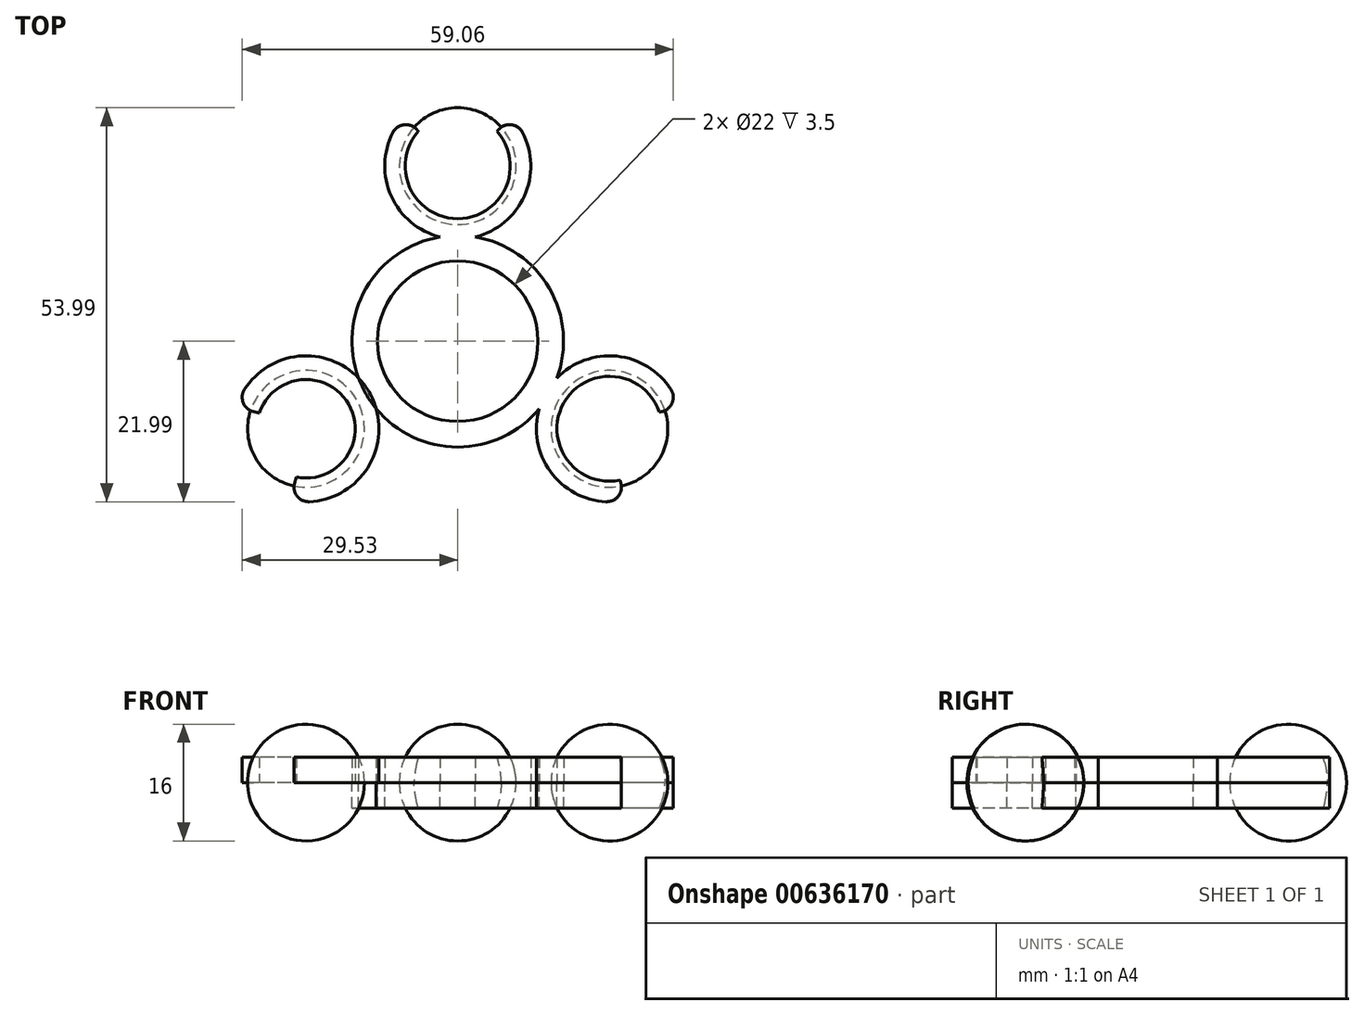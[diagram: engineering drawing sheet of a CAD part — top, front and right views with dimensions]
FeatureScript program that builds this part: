
annotation { "Feature Type Name" : "Feature", "Feature Type Description" : "" }
export const myFeature = defineFeature(function(context is Context, id is Id, definition is map)
    precondition{}
    {
        {
            var Q0;
            Q0=qCreatedBy(makeId("Top.planeOp"),FACE);
            var sketch = newSketch(context, id + "F0", { "sketchPlane" : qUnion([Q0])});
            skCircle(sketch, "E0", {"center": v(0, 0) * mm, "radius": 11 * mm});
            skCircle(sketch, "E1", {"center": v(0, 0) * mm, "radius": 14.5 * mm});
            skArc(sketch, "E2", {"start": v(-5.06, 28.47) * mm, "mid": v(0, 17.25) * mm, "end": v(5.06, 28.47) * mm});
            skArc(sketch, "E3", {"start": v(-6.95, 31.19) * mm, "mid": v(0, 14) * mm, "end": v(6.95, 31.19) * mm});
            skArc(sketch, "E4.1.0", {"start": v(-23.53, -21.61) * mm, "mid": v(-12.12, -7) * mm, "end": v(-30.49, -9.57) * mm});
            skArc(sketch, "E4.1.1", {"start": v(-22.12, -18.62) * mm, "mid": v(-14.94, -8.62) * mm, "end": v(-27.18, -9.85) * mm});
            skArc(sketch, "E4.2.0", {"start": v(30.49, -9.57) * mm, "mid": v(12.12, -7) * mm, "end": v(23.53, -21.61) * mm});
            skArc(sketch, "E4.2.1", {"start": v(27.18, -9.85) * mm, "mid": v(14.94, -8.63) * mm, "end": v(22.12, -18.62) * mm});
            skArc(sketch, "E5", {"start": v(-6.95, 31.19) * mm, "mid": v(-6.16, 29.72) * mm, "end": v(-5.06, 28.47) * mm});
            skArc(sketch, "E6.trimOffspring", {"start": v(5.06, 28.47) * mm, "mid": v(6.16, 29.72) * mm, "end": v(6.95, 31.19) * mm});
            skArc(sketch, "E7.1.0", {"start": v(-27.18, -9.85) * mm, "mid": v(-28.82, -9.53) * mm, "end": v(-30.49, -9.57) * mm});
            skArc(sketch, "E7.1.1", {"start": v(-23.53, -21.61) * mm, "mid": v(-22.66, -20.2) * mm, "end": v(-22.12, -18.62) * mm});
            skArc(sketch, "E7.2.0", {"start": v(22.12, -18.62) * mm, "mid": v(22.66, -20.2) * mm, "end": v(23.53, -21.61) * mm});
            skArc(sketch, "E7.2.1", {"start": v(30.49, -9.57) * mm, "mid": v(28.82, -9.53) * mm, "end": v(27.18, -9.85) * mm});
            skCircle(sketch, "E8", {"center": v(0, 24) * mm, "radius": 8 * mm});
            skLineSegment(sketch, "E9", {"start": v(0, 28.85) * mm, "end": v(0, 20.31) * mm, "construction": true});
            skLineSegment(sketch, "E10", {"start": v(0, 32) * mm, "end": v(0, 16) * mm});
            skPoint(sketch, "E10.endSnap0", {"position": v(0, 17.25) * mm});
            skSolve(sketch);
        }
        {
            var Q0;
            Q0=makeQuery(id+"F0.imprint","IMPRINT",FACE,{"disambiguationData":[TD([[makeQuery(id+"F0.imprint","IMPRINT",EDGE,{"derivedFrom":sQuery(id+"F0.wireOp",EDGE,"E4.1.1")}),-1.0]])]});
            var Q1;
            {var subQ0=sQuery(id+"F0.wireOp",EDGE,"E4.1.0");var subQ1=sQuery(id+"F0.wireOp",EDGE,"E0");var subQ2=makeQuery(id+"F0.imprint","INTERSECT",VERTEX,{"derivedFrom":[subQ1,subQ0]});Q1=makeQuery(id+"F0.imprint","IMPRINT",FACE,{"disambiguationData":[TD([[makeQuery(id+"F0.imprint","IMPRINT",EDGE,{"disambiguationData":[TD([[subQ2,1.0]])],"derivedFrom":subQ1}),-1.0]])]});}
            var Q2;
            {var subQ0=sQuery(id+"F0.wireOp",EDGE,"E4.1.0");var subQ1=sQuery(id+"F0.wireOp",EDGE,"E1");var subQ2=makeQuery(id+"F0.imprint","INTERSECT",VERTEX,{"disambiguationData":[OD(0.0)],"derivedFrom":[subQ1,subQ0]});Q2=makeQuery(id+"F0.imprint","IMPRINT",FACE,{"disambiguationData":[TD([[makeQuery(id+"F0.imprint","IMPRINT",EDGE,{"disambiguationData":[TD([[subQ2,-1.0]])],"derivedFrom":subQ1}),1.0]])]});}
            var Q3;
            {var subQ0=sQuery(id+"F0.wireOp",EDGE,"E4.1.0");var subQ1=sQuery(id+"F0.wireOp",EDGE,"E0");var subQ2=makeQuery(id+"F0.imprint","INTERSECT",VERTEX,{"derivedFrom":[subQ1,subQ0]});Q3=makeQuery(id+"F0.imprint","IMPRINT",FACE,{"disambiguationData":[TD([[makeQuery(id+"F0.imprint","IMPRINT",EDGE,{"disambiguationData":[TD([[subQ2,-1.0]])],"derivedFrom":subQ1}),-1.0]])]});}
            var Q4;
            {var subQ0=sQuery(id+"F0.wireOp",EDGE,"E4.2.0");var subQ1=sQuery(id+"F0.wireOp",EDGE,"E1");var subQ2=makeQuery(id+"F0.imprint","INTERSECT",VERTEX,{"disambiguationData":[OD(0.0)],"derivedFrom":[subQ1,subQ0]});Q4=makeQuery(id+"F0.imprint","IMPRINT",FACE,{"disambiguationData":[TD([[makeQuery(id+"F0.imprint","IMPRINT",EDGE,{"disambiguationData":[TD([[subQ2,-1.0]])],"derivedFrom":subQ1}),1.0]])]});}
            var Q5;
            Q5=makeQuery(id+"F0.imprint","IMPRINT",FACE,{"disambiguationData":[TD([[makeQuery(id+"F0.imprint","IMPRINT",EDGE,{"derivedFrom":sQuery(id+"F0.wireOp",EDGE,"E4.2.1")}),-1.0]])]});
            var Q6;
            {var subQ0=sQuery(id+"F0.wireOp",EDGE,"E3");var subQ1=sQuery(id+"F0.wireOp",EDGE,"E0");var subQ2=makeQuery(id+"F0.imprint","INTERSECT",VERTEX,{"derivedFrom":[subQ1,subQ0]});Q6=makeQuery(id+"F0.imprint","IMPRINT",FACE,{"disambiguationData":[TD([[makeQuery(id+"F0.imprint","IMPRINT",EDGE,{"disambiguationData":[TD([[subQ2,1.0]])],"derivedFrom":subQ1}),-1.0]])]});}
            var Q7;
            {var subQ0=sQuery(id+"F0.wireOp",EDGE,"E3");var subQ1=sQuery(id+"F0.wireOp",EDGE,"E1");var subQ2=makeQuery(id+"F0.imprint","INTERSECT",VERTEX,{"disambiguationData":[OD(0.0)],"derivedFrom":[subQ1,subQ0]});Q7=makeQuery(id+"F0.imprint","IMPRINT",FACE,{"disambiguationData":[TD([[makeQuery(id+"F0.imprint","IMPRINT",EDGE,{"disambiguationData":[TD([[subQ2,1.0]])],"derivedFrom":subQ1}),1.0]])]});}
            var Q8;
            Q8=makeQuery(id+"F0.imprint","IMPRINT",FACE,{"disambiguationData":[TD([[makeQuery(id+"F0.imprint","IMPRINT",EDGE,{"derivedFrom":sQuery(id+"F0.wireOp",EDGE,"E2")}),-1.0]])]});
            var Q9;
            {var subQ1=sQuery(id+"F0.wireOp",EDGE,"E3");var subQ5=sQuery(id+"F0.wireOp",EDGE,"E1");var subQ6=makeQuery(id+"F0.imprint","INTERSECT",VERTEX,{"disambiguationData":[OD(0.0)],"derivedFrom":[subQ5,subQ1]});Q9=makeQuery(id+"F0.imprint","IMPRINT",FACE,{"disambiguationData":[TD([[makeQuery(id+"F0.imprint","IMPRINT",EDGE,{"disambiguationData":[TD([[subQ6,1.0]])],"derivedFrom":subQ5}),-1.0]])]});}
            extrude(context, id + "F1", {"entities" : qUnion([Q0, Q1, Q2, Q3, Q4, Q5, Q6, Q7, Q8, Q9]), "depth" : 3.5 * mm, "offsetDistance" : 25 * mm});
        }
        {
            var Q0;
            {var subQ0=sQuery(id+"F0.wireOp",EDGE,"E6.trimOffspring");var subQ1=sQuery(id+"F0.wireOp",EDGE,"E2");var subQ2=makeQuery(id+"F0.imprint","INTERSECT",VERTEX,{"derivedFrom":[subQ1,subQ0]});Q0=makeQuery(id+"F0.imprint","IMPRINT",FACE,{"disambiguationData":[TD([[makeQuery(id+"F0.imprint","IMPRINT",EDGE,{"disambiguationData":[TD([[subQ2,1.0]])],"derivedFrom":subQ1}),1.0]])]});}
            var Q1;
            {var subQ0=sQuery(id+"F0.wireOp",EDGE,"E6.trimOffspring");var subQ1=sQuery(id+"F0.wireOp",EDGE,"E2");var subQ2=makeQuery(id+"F0.imprint","INTERSECT",VERTEX,{"derivedFrom":[subQ1,subQ0]});Q1=makeQuery(id+"F0.imprint","IMPRINT",FACE,{"disambiguationData":[TD([[makeQuery(id+"F0.imprint","IMPRINT",EDGE,{"disambiguationData":[TD([[subQ2,1.0]])],"derivedFrom":subQ1}),-1.0]])]});}
            var Q2;
            Q2=sQuery(id+"F0.wireOp",EDGE,"E10");
            revolve(context, id + "F2", {"entities" : qUnion([Q0, Q1]), "axis" : qUnion([Q2]), "revolveType" : RevolveType.FULL});
        }
        {
            var Q0;
            Q0=makeQuery(id+"F2.opRevolve","SWEPT_BODY",BODY,{"disambiguationData":[OSD([sQuery(id+"F0.wireOp",EDGE,"E8"),sQuery(id+"F0.wireOp",EDGE,"E10")])]});
            var Q1;
            Q1=sQuery(id+"F0.wireOp",EDGE,"E0");
            circularPattern(context, id + "F3", {"entities" : qUnion([Q0]), "axis" : qUnion([Q1]), "angle" : 360 * degree, "instanceCount" : 3, "equalSpace" : true});
        }
        {
            var Q0;
            Q0=makeQuery(id+"F2.opRevolve","SWEPT_BODY",BODY,{"disambiguationData":[OSD([sQuery(id+"F0.wireOp",EDGE,"E8"),sQuery(id+"F0.wireOp",EDGE,"E10")])]});
            var Q1;
            Q1=makeQuery(id+"F3.opPattern","COPY",BODY,{"derivedFrom":makeQuery(id+"F2.opRevolve","SWEPT_BODY",BODY,{"disambiguationData":[OSD([sQuery(id+"F0.wireOp",EDGE,"E8"),sQuery(id+"F0.wireOp",EDGE,"E10")])]}),"instanceName":"1"});
            var Q2;
            Q2=makeQuery(id+"F3.opPattern","COPY",BODY,{"derivedFrom":makeQuery(id+"F2.opRevolve","SWEPT_BODY",BODY,{"disambiguationData":[OSD([sQuery(id+"F0.wireOp",EDGE,"E8"),sQuery(id+"F0.wireOp",EDGE,"E10")])]}),"instanceName":"2"});
            var Q3;
            Q3=makeQuery(id+"F1.opExtrude","SWEPT_BODY",BODY,{"disambiguationData":[OSD([sQuery(id+"F0.wireOp",EDGE,"E0"),sQuery(id+"F0.wireOp",EDGE,"E1"),sQuery(id+"F0.wireOp",EDGE,"E2"),sQuery(id+"F0.wireOp",EDGE,"E3"),sQuery(id+"F0.wireOp",EDGE,"E4.1.0"),sQuery(id+"F0.wireOp",EDGE,"E4.1.1"),sQuery(id+"F0.wireOp",EDGE,"E4.2.0"),sQuery(id+"F0.wireOp",EDGE,"E4.2.1"),sQuery(id+"F0.wireOp",EDGE,"E5"),sQuery(id+"F0.wireOp",EDGE,"E6.trimOffspring"),sQuery(id+"F0.wireOp",EDGE,"E7.1.0"),sQuery(id+"F0.wireOp",EDGE,"E7.1.1"),sQuery(id+"F0.wireOp",EDGE,"E7.2.0"),sQuery(id+"F0.wireOp",EDGE,"E7.2.1")])]});
            var Q4;
            {var subQ0=sQuery(id+"F0.wireOp",EDGE,"E7.2.1");var subQ1=sQuery(id+"F0.wireOp",EDGE,"E7.2.0");var subQ2=sQuery(id+"F0.wireOp",EDGE,"E7.1.1");var subQ3=sQuery(id+"F0.wireOp",EDGE,"E7.1.0");var subQ4=sQuery(id+"F0.wireOp",EDGE,"E6.trimOffspring");var subQ5=sQuery(id+"F0.wireOp",EDGE,"E3");var subQ6=makeQuery(id+"F0.imprint","INTERSECT",VERTEX,{"derivedFrom":[subQ5,subQ4]});var subQ9=sQuery(id+"F0.wireOp",EDGE,"E2");var subQ10=makeQuery(id+"F0.imprint","INTERSECT",VERTEX,{"derivedFrom":[subQ9,subQ4]});var subQ11=sQuery(id+"F0.wireOp",EDGE,"E5");var subQ12=makeQuery(id+"F0.imprint","INTERSECT",VERTEX,{"derivedFrom":[subQ9,subQ11]});var subQ14=makeQuery(id+"F0.imprint","INTERSECT",VERTEX,{"derivedFrom":[subQ5,subQ11]});var subQ15=sQuery(id+"F0.wireOp",EDGE,"E4.2.1");var subQ16=sQuery(id+"F0.wireOp",EDGE,"E4.2.0");var subQ17=sQuery(id+"F0.wireOp",EDGE,"E1");var subQ20=sQuery(id+"F0.wireOp",EDGE,"E4.1.1");var subQ21=sQuery(id+"F0.wireOp",EDGE,"E4.1.0");var subQ23=makeQuery(id+"F0.imprint","INTERSECT",VERTEX,{"disambiguationData":[OD(1.0)],"derivedFrom":[subQ17,subQ21]});var subQ24=makeQuery(id+"F0.imprint","INTERSECT",VERTEX,{"disambiguationData":[OD(1.0)],"derivedFrom":[subQ17,subQ5]});var subQ25=makeQuery(id+"F0.imprint","INTERSECT",VERTEX,{"disambiguationData":[OD(0.0)],"derivedFrom":[subQ17,subQ5]});var subQ27=sQuery(id+"F0.wireOp",EDGE,"E0");Q4=makeQuery(id+"FuWK4dTKpH4Q4d1_0.opExtrude","SWEPT_BODY",BODY,{"disambiguationData":[OSD([subQ27,subQ17,subQ9,subQ5,subQ21,subQ20,subQ16,subQ15,subQ11,subQ4,subQ3,subQ2,subQ1,subQ0]),TDD([makeQuery(id+"F0.imprint","IMPRINT",EDGE,{"derivedFrom":subQ27}),makeQuery(id+"F0.imprint","IMPRINT",EDGE,{"disambiguationData":[TD([[subQ25,-1.0]])],"derivedFrom":subQ17}),makeQuery(id+"F0.imprint","IMPRINT",EDGE,{"disambiguationData":[TD([[subQ23,-1.0]])],"derivedFrom":subQ17}),makeQuery(id+"F0.imprint","IMPRINT",EDGE,{"disambiguationData":[TD([[subQ24,1.0]])],"derivedFrom":subQ17}),makeQuery(id+"F0.imprint","IMPRINT",EDGE,{"disambiguationData":[TD([[subQ12,-1.0]])],"derivedFrom":subQ9}),makeQuery(id+"F0.imprint","IMPRINT",EDGE,{"disambiguationData":[TD([[subQ10,1.0]])],"derivedFrom":subQ9}),makeQuery(id+"F0.imprint","IMPRINT",EDGE,{"disambiguationData":[TD([[subQ14,-1.0]])],"derivedFrom":subQ5}),makeQuery(id+"F0.imprint","IMPRINT",EDGE,{"disambiguationData":[TD([[subQ6,1.0]])],"derivedFrom":subQ5}),makeQuery(id+"F0.imprint","IMPRINT",EDGE,{"disambiguationData":[TD([[makeQuery(id+"F0.imprint","INTERSECT",VERTEX,{"derivedFrom":[subQ21,subQ2]}),-1.0]])],"derivedFrom":subQ21}),makeQuery(id+"F0.imprint","IMPRINT",EDGE,{"disambiguationData":[TD([[makeQuery(id+"F0.imprint","INTERSECT",VERTEX,{"derivedFrom":[subQ21,subQ3]}),1.0]])],"derivedFrom":subQ21}),makeQuery(id+"F0.imprint","IMPRINT",EDGE,{"derivedFrom":subQ20}),makeQuery(id+"F0.imprint","IMPRINT",EDGE,{"disambiguationData":[TD([[makeQuery(id+"F0.imprint","INTERSECT",VERTEX,{"derivedFrom":[subQ16,subQ0]}),-1.0]])],"derivedFrom":subQ16}),makeQuery(id+"F0.imprint","IMPRINT",EDGE,{"disambiguationData":[TD([[makeQuery(id+"F0.imprint","INTERSECT",VERTEX,{"derivedFrom":[subQ16,subQ1]}),1.0]])],"derivedFrom":subQ16}),makeQuery(id+"F0.imprint","IMPRINT",EDGE,{"derivedFrom":subQ15}),makeQuery(id+"F0.imprint","IMPRINT",EDGE,{"disambiguationData":[TD([[subQ14,-1.0]])],"derivedFrom":subQ11}),makeQuery(id+"F0.imprint","IMPRINT",EDGE,{"disambiguationData":[TD([[subQ12,1.0]])],"derivedFrom":subQ11}),makeQuery(id+"F0.imprint","IMPRINT",EDGE,{"disambiguationData":[TD([[subQ10,-1.0]])],"derivedFrom":subQ4}),makeQuery(id+"F0.imprint","IMPRINT",EDGE,{"disambiguationData":[TD([[subQ6,1.0]])],"derivedFrom":subQ4}),makeQuery(id+"F0.imprint","IMPRINT",EDGE,{"derivedFrom":subQ3}),makeQuery(id+"F0.imprint","IMPRINT",EDGE,{"derivedFrom":subQ2}),makeQuery(id+"F0.imprint","IMPRINT",EDGE,{"derivedFrom":subQ1}),makeQuery(id+"F0.imprint","IMPRINT",EDGE,{"derivedFrom":subQ0})])]});}
            booleanBodies(context, id + "F4", {"operationType" : BooleanOperationType.INTERSECTION, "tools" : qUnion([Q0, Q1, Q2, Q3, Q4]), "keepTools" : true});
        }
        {
            var Q0;
            Q0=makeQuery(id+"F1.opExtrude","SWEPT_EDGE",EDGE,{"disambiguationData":[OSD([sQuery(id+"F0.wireOp",EDGE,"E4.1.0"),sQuery(id+"F0.wireOp",EDGE,"E7.1.0")])]});
            var Q1;
            Q1=makeQuery(id+"F1.opExtrude","SWEPT_EDGE",EDGE,{"disambiguationData":[OSD([sQuery(id+"F0.wireOp",EDGE,"E4.1.0"),sQuery(id+"F0.wireOp",EDGE,"E7.1.1")])]});
            var Q2;
            {var subQ0=sQuery(id+"F0.wireOp",EDGE,"E7.1.0");var subQ1=sQuery(id+"F0.wireOp",EDGE,"E4.1.0");Q2=makeQuery(id+"FuWK4dTKpH4Q4d1_0.opExtrude","SWEPT_EDGE",EDGE,{"disambiguationData":[OSD([subQ1,subQ0]),TDD([makeQuery(id+"F0.imprint","INTERSECT",VERTEX,{"derivedFrom":[subQ1,subQ0]})])]});}
            var Q3;
            {var subQ0=sQuery(id+"F0.wireOp",EDGE,"E7.1.1");var subQ1=sQuery(id+"F0.wireOp",EDGE,"E4.1.0");Q3=makeQuery(id+"FuWK4dTKpH4Q4d1_0.opExtrude","SWEPT_EDGE",EDGE,{"disambiguationData":[OSD([subQ1,subQ0]),TDD([makeQuery(id+"F0.imprint","INTERSECT",VERTEX,{"derivedFrom":[subQ1,subQ0]})])]});}
            var Q4;
            Q4=makeQuery(id+"F1.opExtrude","SWEPT_EDGE",EDGE,{"disambiguationData":[OSD([sQuery(id+"F0.wireOp",EDGE,"E4.2.0"),sQuery(id+"F0.wireOp",EDGE,"E7.2.0")])]});
            var Q5;
            {var subQ0=sQuery(id+"F0.wireOp",EDGE,"E7.2.0");var subQ1=sQuery(id+"F0.wireOp",EDGE,"E4.2.0");Q5=makeQuery(id+"FuWK4dTKpH4Q4d1_0.opExtrude","SWEPT_EDGE",EDGE,{"disambiguationData":[OSD([subQ1,subQ0]),TDD([makeQuery(id+"F0.imprint","INTERSECT",VERTEX,{"derivedFrom":[subQ1,subQ0]})])]});}
            var Q6;
            Q6=makeQuery(id+"F1.opExtrude","SWEPT_EDGE",EDGE,{"disambiguationData":[OSD([sQuery(id+"F0.wireOp",EDGE,"E4.2.0"),sQuery(id+"F0.wireOp",EDGE,"E7.2.1")])]});
            var Q7;
            {var subQ0=sQuery(id+"F0.wireOp",EDGE,"E7.2.1");var subQ1=sQuery(id+"F0.wireOp",EDGE,"E4.2.0");Q7=makeQuery(id+"FuWK4dTKpH4Q4d1_0.opExtrude","SWEPT_EDGE",EDGE,{"disambiguationData":[OSD([subQ1,subQ0]),TDD([makeQuery(id+"F0.imprint","INTERSECT",VERTEX,{"derivedFrom":[subQ1,subQ0]})])]});}
            var Q8;
            Q8=makeQuery(id+"F1.opExtrude","SWEPT_EDGE",EDGE,{"disambiguationData":[OSD([sQuery(id+"F0.wireOp",EDGE,"E3"),sQuery(id+"F0.wireOp",EDGE,"E6.trimOffspring")])]});
            var Q9;
            {var subQ0=sQuery(id+"F0.wireOp",EDGE,"E6.trimOffspring");var subQ1=sQuery(id+"F0.wireOp",EDGE,"E3");Q9=makeQuery(id+"FuWK4dTKpH4Q4d1_0.opExtrude","SWEPT_EDGE",EDGE,{"disambiguationData":[OSD([subQ1,subQ0]),TDD([makeQuery(id+"F0.imprint","INTERSECT",VERTEX,{"derivedFrom":[subQ1,subQ0]})])]});}
            var Q10;
            {var subQ0=sQuery(id+"F0.wireOp",EDGE,"E5");var subQ1=sQuery(id+"F0.wireOp",EDGE,"E3");Q10=makeQuery(id+"FuWK4dTKpH4Q4d1_0.opExtrude","SWEPT_EDGE",EDGE,{"disambiguationData":[OSD([subQ1,subQ0]),TDD([makeQuery(id+"F0.imprint","INTERSECT",VERTEX,{"derivedFrom":[subQ1,subQ0]})])]});}
            var Q11;
            Q11=makeQuery(id+"F1.opExtrude","SWEPT_EDGE",EDGE,{"disambiguationData":[OSD([sQuery(id+"F0.wireOp",EDGE,"E3"),sQuery(id+"F0.wireOp",EDGE,"E5")])]});
            fillet(context, id + "F5", {"entities" : qUnion([Q0, Q1, Q2, Q3, Q4, Q5, Q6, Q7, Q8, Q9, Q10, Q11]), "radius" : 2 * mm, "tangentPropagation" : true, "allowEdgeOverflow" : false});
        }
        {
            var Q0;
            Q0=makeQuery(id+"F2.opRevolve","SWEPT_BODY",BODY,{"disambiguationData":[OSD([sQuery(id+"F0.wireOp",EDGE,"E8"),sQuery(id+"F0.wireOp",EDGE,"E10")])]});
            var Q1;
            Q1=makeQuery(id+"F3.opPattern","COPY",BODY,{"derivedFrom":makeQuery(id+"F2.opRevolve","SWEPT_BODY",BODY,{"disambiguationData":[OSD([sQuery(id+"F0.wireOp",EDGE,"E8"),sQuery(id+"F0.wireOp",EDGE,"E10")])]}),"instanceName":"1"});
            var Q2;
            Q2=makeQuery(id+"F3.opPattern","COPY",BODY,{"derivedFrom":makeQuery(id+"F2.opRevolve","SWEPT_BODY",BODY,{"disambiguationData":[OSD([sQuery(id+"F0.wireOp",EDGE,"E8"),sQuery(id+"F0.wireOp",EDGE,"E10")])]}),"instanceName":"2"});
            var Q3;
            Q3=makeQuery(id+"F1.opExtrude","SWEPT_BODY",BODY,{"disambiguationData":[OSD([sQuery(id+"F0.wireOp",EDGE,"E0"),sQuery(id+"F0.wireOp",EDGE,"E1"),sQuery(id+"F0.wireOp",EDGE,"E2"),sQuery(id+"F0.wireOp",EDGE,"E3"),sQuery(id+"F0.wireOp",EDGE,"E4.1.0"),sQuery(id+"F0.wireOp",EDGE,"E4.1.1"),sQuery(id+"F0.wireOp",EDGE,"E4.2.0"),sQuery(id+"F0.wireOp",EDGE,"E4.2.1"),sQuery(id+"F0.wireOp",EDGE,"E5"),sQuery(id+"F0.wireOp",EDGE,"E6.trimOffspring"),sQuery(id+"F0.wireOp",EDGE,"E7.1.0"),sQuery(id+"F0.wireOp",EDGE,"E7.1.1"),sQuery(id+"F0.wireOp",EDGE,"E7.2.0"),sQuery(id+"F0.wireOp",EDGE,"E7.2.1")])]});
            booleanBodies(context, id + "F6", {"operationType" : BooleanOperationType.SUBTRACTION, "tools" : qUnion([Q0, Q1, Q2]), "targets" : qUnion([Q3]), "keepTools" : true});
        }
        {
            var Q0;
            Q0=makeQuery(id+"F1.opExtrude","SWEPT_BODY",BODY,{"disambiguationData":[OSD([sQuery(id+"F0.wireOp",EDGE,"E0"),sQuery(id+"F0.wireOp",EDGE,"E1"),sQuery(id+"F0.wireOp",EDGE,"E2"),sQuery(id+"F0.wireOp",EDGE,"E3"),sQuery(id+"F0.wireOp",EDGE,"E4.1.0"),sQuery(id+"F0.wireOp",EDGE,"E4.1.1"),sQuery(id+"F0.wireOp",EDGE,"E4.2.0"),sQuery(id+"F0.wireOp",EDGE,"E4.2.1"),sQuery(id+"F0.wireOp",EDGE,"E5"),sQuery(id+"F0.wireOp",EDGE,"E6.trimOffspring"),sQuery(id+"F0.wireOp",EDGE,"E7.1.0"),sQuery(id+"F0.wireOp",EDGE,"E7.1.1"),sQuery(id+"F0.wireOp",EDGE,"E7.2.0"),sQuery(id+"F0.wireOp",EDGE,"E7.2.1")])]});
            var Q1;
            Q1=makeQuery(id+"F1.opExtrude","CAP_FACE",FACE,{"disambiguationData":[OSD([sQuery(id+"F0.wireOp",EDGE,"E0"),sQuery(id+"F0.wireOp",EDGE,"E1"),sQuery(id+"F0.wireOp",EDGE,"E2"),sQuery(id+"F0.wireOp",EDGE,"E3"),sQuery(id+"F0.wireOp",EDGE,"E4.1.0"),sQuery(id+"F0.wireOp",EDGE,"E4.1.1"),sQuery(id+"F0.wireOp",EDGE,"E4.2.0"),sQuery(id+"F0.wireOp",EDGE,"E4.2.1"),sQuery(id+"F0.wireOp",EDGE,"E5"),sQuery(id+"F0.wireOp",EDGE,"E6.trimOffspring"),sQuery(id+"F0.wireOp",EDGE,"E7.1.0"),sQuery(id+"F0.wireOp",EDGE,"E7.1.1"),sQuery(id+"F0.wireOp",EDGE,"E7.2.0"),sQuery(id+"F0.wireOp",EDGE,"E7.2.1")])],"isStart":true});
            mirror(context, id + "F7", {"entities" : qUnion([Q0]), "mirrorPlane" : qUnion([Q1])});
        }
    });
